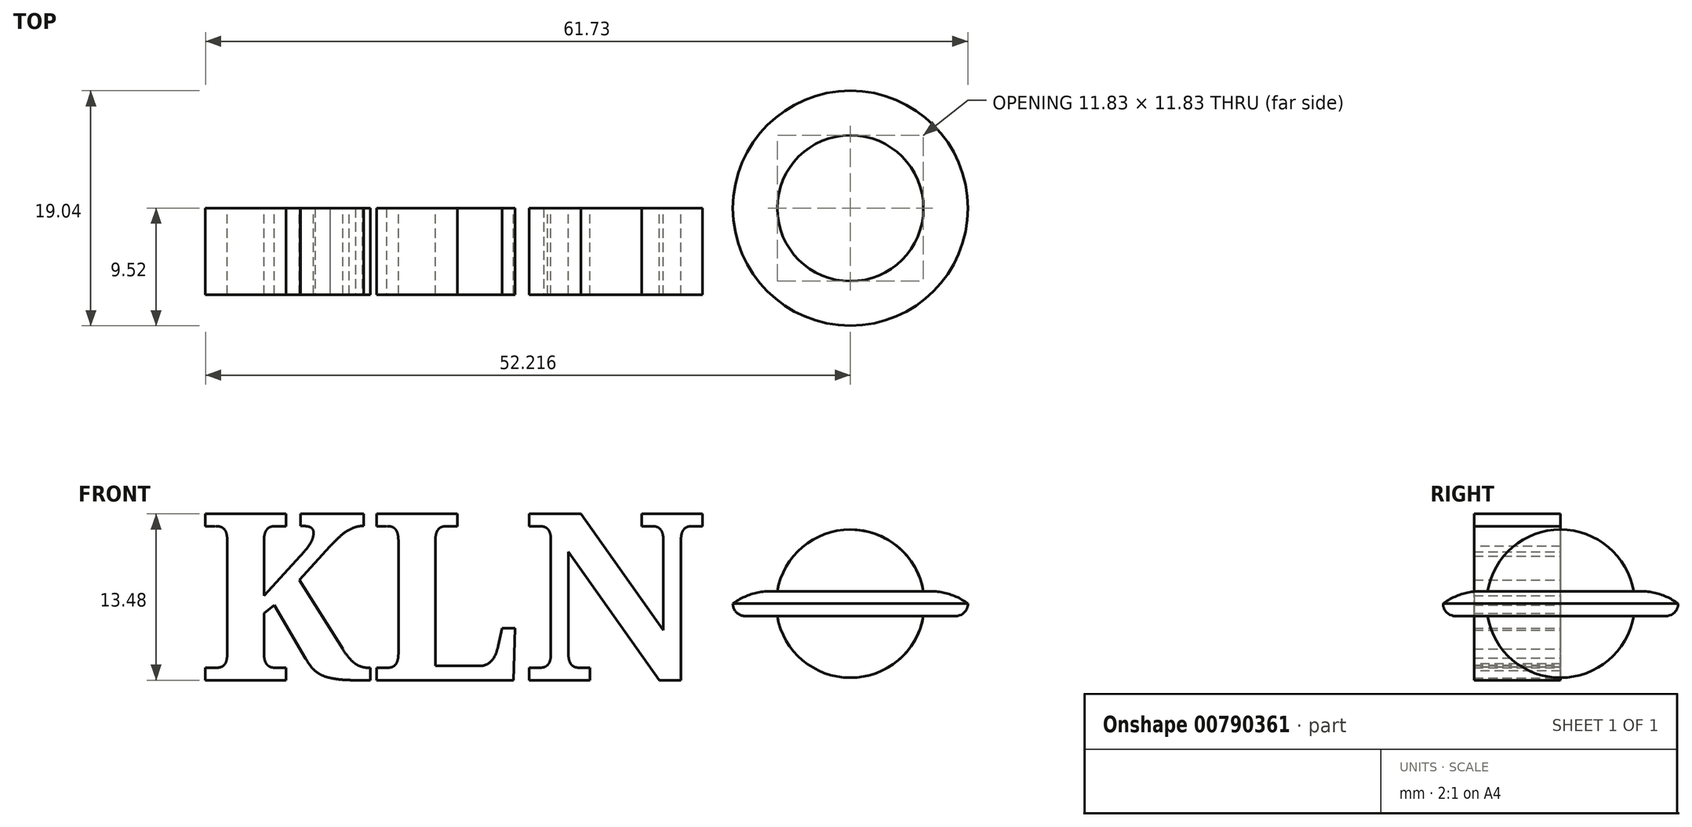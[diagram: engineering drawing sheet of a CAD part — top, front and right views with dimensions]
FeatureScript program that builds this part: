
annotation { "Feature Type Name" : "Feature", "Feature Type Description" : "" }
export const myFeature = defineFeature(function(context is Context, id is Id, definition is map)
    precondition{}
    {
        {
            var Q0;
            Q0=qCreatedBy(makeId("Front.planeOp"),FACE);
            var sketch = newSketch(context, id + "F0", { "sketchPlane" : qUnion([Q0])});
            skText(sketch, "E0", { "text": "KLN\n", "fontName": "NotoSerif-Bold.ttf"});
            const initialGuessF0  = {"E0": [-0.02548, 0, 1, 0, 0.0136]};
            skSetInitialGuess(sketch, initialGuessF0);
            skSolve(sketch);
        }
        {
            var Q0;
            Q0=makeQuery(id+"F0.imprint","IMPRINT",FACE,{"disambiguationData":[TD([[makeQuery(id+"F0.imprint","IMPRINT",EDGE,{"derivedFrom":sQuery(id+"F0.wireOp",EDGE,"E0.sketch_text.stroke-0")}),-1.0]])]});
            var Q1;
            Q1=makeQuery(id+"F0.imprint","IMPRINT",FACE,{"disambiguationData":[TD([[makeQuery(id+"F0.imprint","IMPRINT",EDGE,{"derivedFrom":sQuery(id+"F0.wireOp",EDGE,"E0.sketch_text.stroke-60")}),-1.0]])]});
            var Q2;
            Q2=makeQuery(id+"F0.imprint","IMPRINT",FACE,{"disambiguationData":[TD([[makeQuery(id+"F0.imprint","IMPRINT",EDGE,{"derivedFrom":sQuery(id+"F0.wireOp",EDGE,"E0.sketch_text.stroke-88")}),-1.0]])]});
            extrude(context, id + "F1", {"entities" : qUnion([Q0, Q1, Q2]), "depth" : 7 * mm, "offsetDistance" : 25 * mm});
        }
        {
            var Q0;
            Q0=qCreatedBy(makeId("Front.planeOp"),FACE);
            var sketch = newSketch(context, id + "F2", { "sketchPlane" : qUnion([Q0])});
            skLineSegment(sketch, "E1", {"start": v(27.27, 6.2) * mm, "end": v(33.27, 6.2) * mm});
            skArc(sketch, "E2", {"start": v(33.27, 6.2) * mm, "mid": v(31.5, 10.45) * mm, "end": v(27.27, 12.2) * mm});
            skLineSegment(sketch, "E3", {"start": v(33.27, 6.2) * mm, "end": v(36.78, 6.2) * mm});
            skLineSegment(sketch, "E4", {"start": v(36.78, 6.2) * mm, "end": v(36.78, 7.2) * mm});
            skLineSegment(sketch, "E5", {"start": v(36.78, 7.2) * mm, "end": v(33.18, 7.2) * mm});
            skLineSegment(sketch, "E6", {"start": v(27.27, 6.2) * mm, "end": v(27.27, 12.2) * mm});
            skPoint(sketch, "E7.orphan", {"position": v(21.27, 6.2) * mm});
            skSolve(sketch);
        }
        {
            var Q0;
            Q0 = qSketchRegion(id + "F2", true);
            var Q1;
            Q1=sQuery(id+"F2.wireOp",EDGE,"E6");
            revolve(context, id + "F3", {"surfaceOperationType" : NewSurfaceOperationType.NEW, "entities" : qUnion([Q0]), "axis" : qUnion([Q1]), "revolveType" : RevolveType.FULL});
        }
        {
            var Q0;
            Q0=makeQuery(id+"F3.opRevolve","SWEPT_BODY",BODY,{"disambiguationData":[OSD([sQuery(id+"F2.wireOp",EDGE,"E1"),sQuery(id+"F2.wireOp",EDGE,"E2"),sQuery(id+"F2.wireOp",EDGE,"E3"),sQuery(id+"F2.wireOp",EDGE,"E4"),sQuery(id+"F2.wireOp",EDGE,"E5"),sQuery(id+"F2.wireOp",EDGE,"E6")])]});
            var Q1;
            Q1=makeQuery(id+"F3.opRevolve","SWEPT_FACE",FACE,{"disambiguationData":[OSD([sQuery(id+"F2.wireOp",EDGE,"E1"),sQuery(id+"F2.wireOp",EDGE,"E3")])]});
            mirror(context, id + "F4", {"operationType" : NewBodyOperationType.ADD, "entities" : qUnion([Q0]), "mirrorPlane" : qUnion([Q1])});
        }
        {
            var Q0;
            Q0=makeQuery(id+"F3.opRevolve","SWEPT_EDGE",EDGE,{"disambiguationData":[OSD([sQuery(id+"F2.wireOp",EDGE,"E4"),sQuery(id+"F2.wireOp",EDGE,"E5")])]});
            fillet(context, id + "F5", {"entities" : qUnion([Q0]), "radius" : 5 * mm, "tangentPropagation" : true, "allowEdgeOverflow" : false});
        }
        {
            var Q0;
            Q0=makeQuery(id+"F3.opRevolve","SWEPT_EDGE",EDGE,{"disambiguationData":[OSD([sQuery(id+"F2.wireOp",EDGE,"E4"),sQuery(id+"F2.wireOp",EDGE,"E5")])]});
            var Q1;
            Q1=makeQuery(id+"F4.opPattern","COPY",EDGE,{"derivedFrom":makeQuery(id+"F3.opRevolve","SWEPT_EDGE",EDGE,{"disambiguationData":[OSD([sQuery(id+"F2.wireOp",EDGE,"E4"),sQuery(id+"F2.wireOp",EDGE,"E5")])]}),"instanceName":"1"});
            fillet(context, id + "F6", {"entities" : qUnion([Q0, Q1]), "radius" : 1 * mm, "tangentPropagation" : true, "allowEdgeOverflow" : false});
        }
    });
